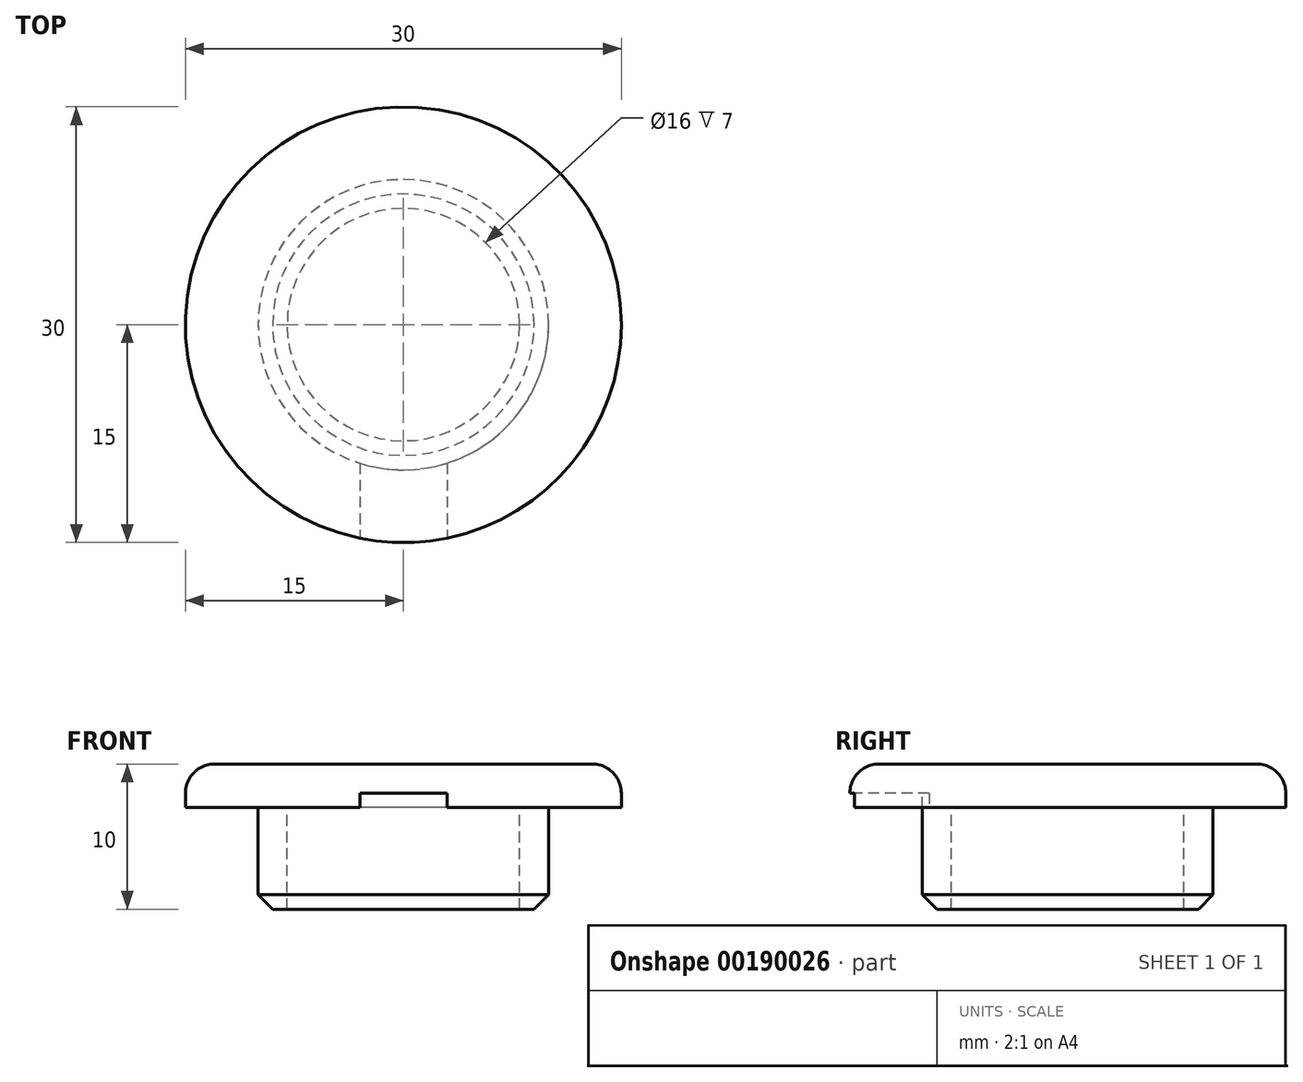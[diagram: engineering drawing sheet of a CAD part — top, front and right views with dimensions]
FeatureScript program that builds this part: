
annotation { "Feature Type Name" : "Feature", "Feature Type Description" : "" }
export const myFeature = defineFeature(function(context is Context, id is Id, definition is map)
    precondition{}
    {
        {
            var Q0;
            Q0=qCreatedBy(makeId("Top.planeOp"),FACE);
            var sketch = newSketch(context, id + "F0", { "sketchPlane" : qUnion([Q0])});
            skCircle(sketch, "E0", {"center": v(0, 0) * mm, "radius": 10 * mm});
            skCircle(sketch, "E1.0", {"center": v(0, 0) * mm, "radius": 8 * mm});
            skCircle(sketch, "E2.0", {"center": v(0, 0) * mm, "radius": 15 * mm});
            skLineSegment(sketch, "E3", {"start": v(0, 0) * mm, "end": v(0, -15) * mm, "construction": true});
            skLineSegment(sketch, "E4.0", {"start": v(-3, -9.54) * mm, "end": v(-3, -14.7) * mm});
            skLineSegment(sketch, "E5.0", {"start": v(3, -9.54) * mm, "end": v(3, -14.7) * mm});
            skSolve(sketch);
        }
        {
            var Q0;
            Q0 = qSketchRegion(id + "F0", true);
            var Q1;
            Q1=makeQuery(id+"F0.imprint","IMPRINT",FACE,{"disambiguationData":[TD([[makeQuery(id+"F0.imprint","IMPRINT",EDGE,{"derivedFrom":sQuery(id+"F0.wireOp",EDGE,"E0")}),1.0]])]});
            var Q2;
            Q2=makeQuery(id+"F0.imprint","IMPRINT",FACE,{"disambiguationData":[TD([[makeQuery(id+"F0.imprint","IMPRINT",EDGE,{"derivedFrom":sQuery(id+"F0.wireOp",EDGE,"E1.0")}),1.0]])]});
            extrude(context, id + "F1", {"entities" : qUnion([Q0, Q1, Q2]), "depth" : 3 * mm});
        }
        {
            var Q0;
            Q0=makeQuery(id+"F0.imprint","IMPRINT",FACE,{"disambiguationData":[TD([[makeQuery(id+"F0.imprint","IMPRINT",EDGE,{"derivedFrom":sQuery(id+"F0.wireOp",EDGE,"E0")}),1.0]])]});
            extrude(context, id + "F2", {"entities" : qUnion([Q0]), "operationType" : NewBodyOperationType.ADD, "oppositeDirection" : true, "depth" : 7 * mm});
        }
        {
            var Q0;
            Q0=makeQuery(id+"F1.opExtrude","CAP_EDGE",EDGE,{"disambiguationData":[OSD([sQuery(id+"F0.wireOp",EDGE,"E2.0")])],"isStart":false});
            fillet(context, id + "F3", {"entities" : qUnion([Q0]), "radius" : 2 * mm, "tangentPropagation" : true, "allowEdgeOverflow" : false});
        }
        {
            var Q0;
            Q0=makeQuery(id+"F2.opExtrude","CAP_EDGE",EDGE,{"disambiguationData":[OSD([sQuery(id+"F0.wireOp",EDGE,"E0")])],"isStart":false});
            chamfer(context, id + "F4", {"entities" : qUnion([Q0]), "width" : 1 * mm, "tangentPropagation" : true});
        }
        {
            var Q0;
            {var subQ0=sQuery(id+"F0.wireOp",EDGE,"E4.0");Q0=makeQuery(id+"F0.imprint","IMPRINT",FACE,{"disambiguationData":[TD([[makeQuery(id+"F0.imprint","IMPRINT",EDGE,{"derivedFrom":subQ0}),1.0]])]});}
            extrude(context, id + "F5", {"entities" : qUnion([Q0]), "operationType" : NewBodyOperationType.REMOVE, "depth" : 1 * mm});
        }
    });
